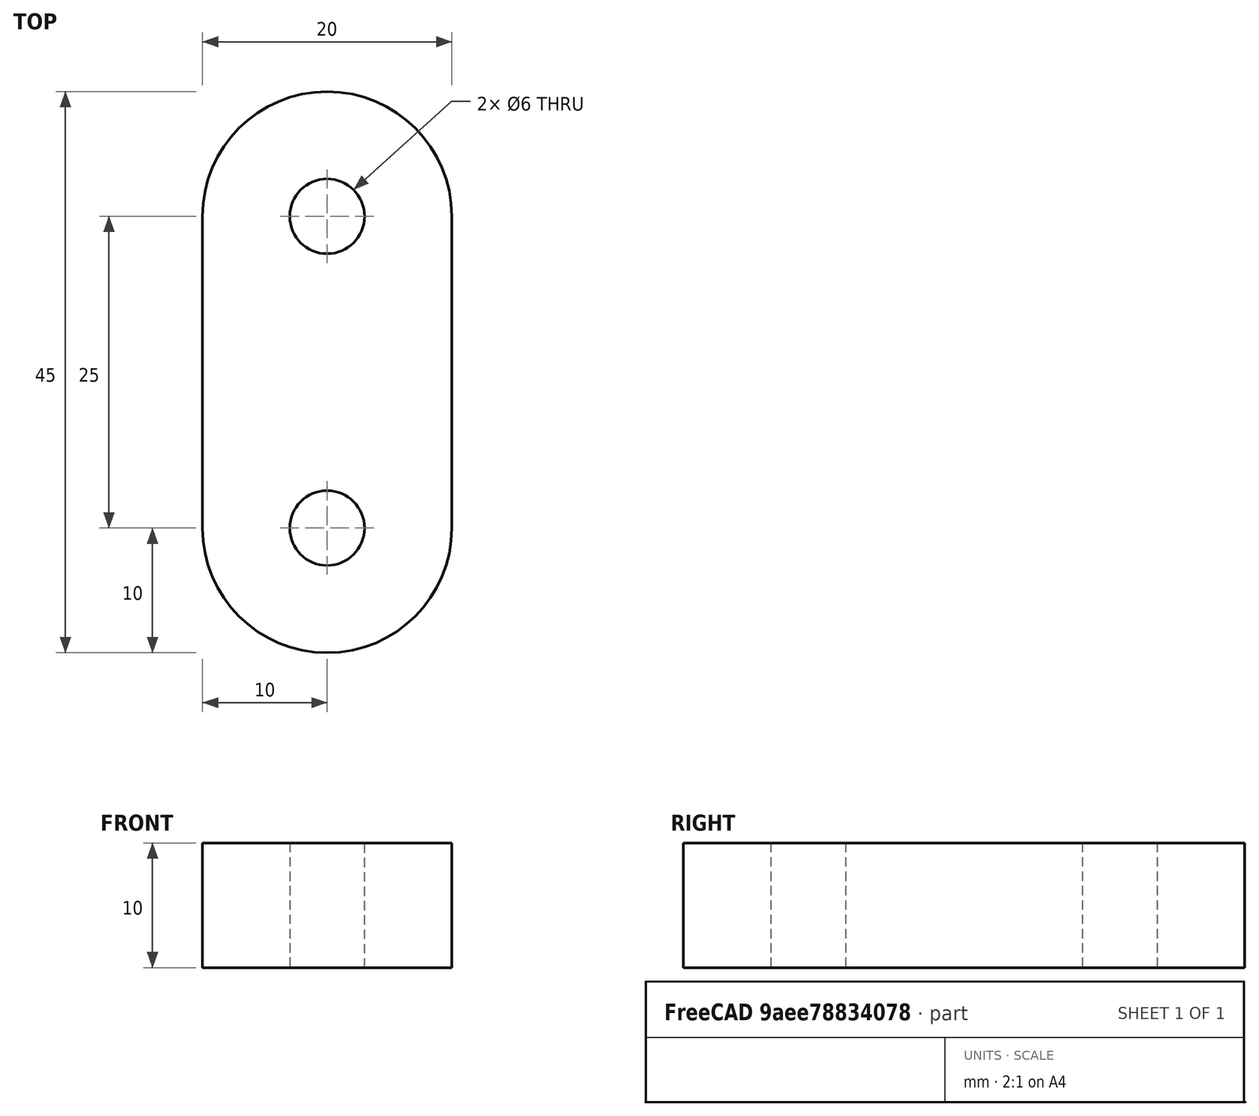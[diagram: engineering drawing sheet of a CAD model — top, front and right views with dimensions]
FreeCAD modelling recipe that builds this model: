
FCSTD DOCUMENT  (FreeCAD 0.19R23756 (Git))
Label: CLAMP_5
License: All rights reserved
LicenseURL: http://en.wikipedia.org/wiki/All_rights_reserved
objects: Sketcher::SketchObject×1, PartDesign::Pad×1, PartDesign::Body×1
note: 4 computed .brp shape members not serialized (recipe doc carries the construction recipe); baked Part::Feature solids carry a one-line shape summary decoded from their .brp

FEATURE [Sketcher::SketchObject] Sketch
  FullyConstrained = true
  MapMode = 5
  Support = -> [XY_Plane]
  sketch-geometry (6):
    g0: ArcOfCircle CenterX=0 CenterY=0 CenterZ=0 NormalX=0 NormalY=0 NormalZ=1 AngleXU=0 Radius=10 StartAngle=3.14159 EndAngle=6.28319
    g1: ArcOfCircle CenterX=0 CenterY=25 CenterZ=0 NormalX=0 NormalY=0 NormalZ=1 AngleXU=0 Radius=10 StartAngle=4.98093e-11 EndAngle=3.14159
    g2: LineSegment StartX=10 StartY=-4.98093e-10 StartZ=0 EndX=10 EndY=25 EndZ=0
    g3: LineSegment StartX=-10 StartY=-4.98094e-10 StartZ=0 EndX=-10 EndY=25 EndZ=0
    g4: Circle CenterX=0 CenterY=25 CenterZ=0 NormalX=0 NormalY=0 NormalZ=1 AngleXU=0 Radius=3
    g5: Circle CenterX=0 CenterY=0 CenterZ=0 NormalX=0 NormalY=0 NormalZ=1 AngleXU=0 Radius=3
  constraints (13):
    c: Tangent(g0,g3) = 1.5708
    c: Tangent(g0,g2) = -1.5708
    c: Tangent(g2,g1) = -1.5708
    c: Tangent(g3,g1) = 1.5708
    c: Vertical(g2)
    c: Equal(g0,g1)
    c: Coincident(g0,g-1)
    c: Radius(g1) = 10
    c: DistanceY(g0,g1) = 25
    c: Coincident(g4,g1)
    c: Coincident(g5,g0)
    c: Equal(g4,g5)
    c: Diameter(g4) = 6
FEATURE [PartDesign::Pad] Pad
  AllowMultiFace = false
  Direction = (1,1,1)
  Length = 10
  Length2 = 100
  Profile = -> Sketch
  Type = 0
FEATURE [PartDesign::Body] Body
  Group = -> [Sketch,Pad]
  Origin = -> Origin
  Tip = -> Pad
